# Revit family: VLN_Nim-II-Mes-E_F3059_BIM_NL
name_source: partatom
category: Plumbing Fixtures
revit_build: Autodesk Revit MEP 2014 (Build: 20130308_1515(x64)
units: mm (PartAtom-declared; Revit-internal decimal feet)

## types (1)
- F3059AA - NIM-II-MES-E DOUCHE M KR 120 OMST CHR
    Accessories = www.idealstandardnederland.nl
    AreaUnits = millimeters
    Assembly Code = C1030200
    AssetType = Vast
    BIMObjectName = VLN_Venlo_ShowerManualWaterSupplySets_F3059AA
    BREEAMApproved = No
    BarCode = 8711678062970
    Brand = Venlo
    CWFU = 0
    CodePerformance = EN 817, DIN 4109
    Color = Chroom
    ConnectionType = Sanitair
    Cost = 0 $
    Default Elevation = 800 mm  [stored 2.62467 ft]
    Description = Venlo Nimbus II Messing douchemengkraan eco. H.o.h. 120 mm. Draaibare onderuitloop. Straalregelaar. Omstelling. Aansluiting G1/2". Eco bovendelen. Exclusief S-koppelingen en rozetten.
    DurationUnit = jaar
    ECA = No
    ExpectedLife = 25
    FaucetFunction = Mengkraan
    FaucetOperation = Tweegreeps
    FaucetType = Douchemengkraan
    Features = Douchemengkraan eco. H.o.h. 120 mm. Draaibare onderuitloop. Straalregelaar. Omstelling. Aansluiting G1/2". Eco bovendelen. Exclusief S-koppelingen en rozetten.
    Finish = Chroom
    FlowRate = 7,6 liter @ 3 bar
    HWFU = 0
    IfcExportAs = IfcValveType
    IfcExportType = FAUCET
    InstallationInstructions = http://www.idealstandardnederland.nl
    LinearUnits = millimeters
    ManufacturerURL = www.idealstandardnederland.nl
    Material = Messing
    Model = F3059AA
    ModelNumber = F3059AA
    ModelReference = Venlo Nimbus II Messing douchemengkraan eco. H.o.h. 120 mm. Draaibare onderuitloop. Straalregelaar. Omstelling. Aansluiting G1/2". Eco bovendelen. Exclusief S-koppelingen en rozetten.
    NBSDescription = Shower mixers
    NBSReference = 45-35-70/335
    Name = ShowerManualWaterSupplySets_F3059AA_Venlo
    NettWeight = 1.181 kg
    NominalHeight = 164 mm
    NominalLength = 184 mm
    NominalWidth = 157 mm
    ProductInformation = http://www.idealstandardnederland.nl
    Shape = Gesculptuurd
    Size = 157 x 184 x 164 mm
    Space = Internal
    SpareParts = www.idealstandardnederland.nl
    TMV3 = Yes
    TestPressure = 10 Bar
    URL = www.idealstandardnederland.nl
    Uniclass2015Code = Pr_40_20_87_78
    Uniclass2015Title = Shower manual water supply sets
    Uniclass2015Version = Products v1.1
    ValveMechanism = Keramische schijven
    ValveOperation = Tweegreeps
    Version = 1
    VolumeUnits = liter
    WFU = 0
    WRAS = No
    WarrantyDescription = Fabrieksgarantie
    WarrantyDurationParts = 10
    WarrantyDurationUnit = jaar
    WaterEfficientProduct = No
    WorkingPressure = 1-5 bar

note: [stored X ft] marks values corroborated as IEEE doubles in the binary element streams (Revit-internal decimal feet)

## geometry (parser evidence)
native form markers: Sweep x1
no freeform markers — native parametric forms only
